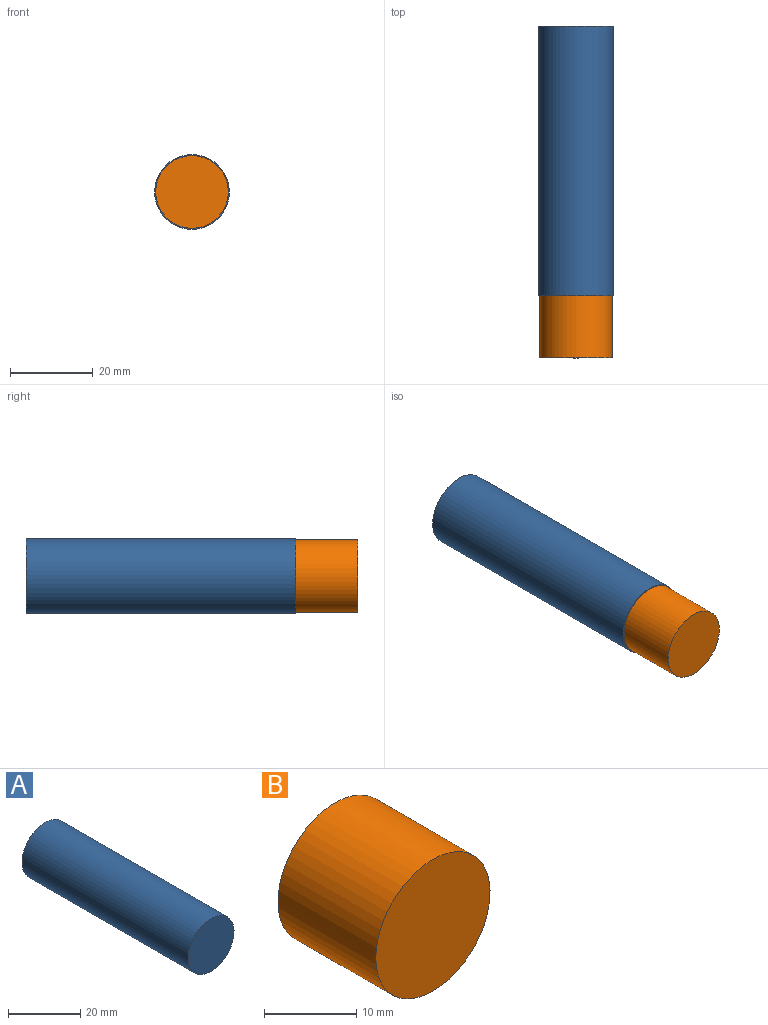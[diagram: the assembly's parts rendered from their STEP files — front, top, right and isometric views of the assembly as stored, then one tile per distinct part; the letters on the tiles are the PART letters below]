
ASSEMBLY  parts=2 mates=1
PART A: 3 faces, bbox 18x65x18 mm
  f0: cylinder r=9mm len=65mm, axis (0,1,0), area 3675.7mm2, adj f1,f2
  f1: plane 18x18mm, normal (0,-1,0), area 254.5mm2, adj f0
  f2: plane 18x18mm, normal (0,1,0), area 254.5mm2, adj f0
PART B: 3 faces, bbox 17.5x15x17.5 mm
  f0: cylinder r=8.75mm len=17.5mm, axis (0,1,0), area 824.7mm2, adj f1,f2
  f1: plane 17.5x17.5mm, normal (0,-1,0), area 240.5mm2, adj f0
  f2: plane 17.5x17.5mm, normal (0,1,0), area 240.5mm2, adj f0
PLACE A t=(9.73,40.4,3.43)mm
PLACE B rot(axis=(1,0,0),180deg) t=(9.73,-39.6,3.43)mm
MATE fastened B.f0 <-> A.f0  axis (0,1,0) through (9.73,-24.6,3.43)mm
